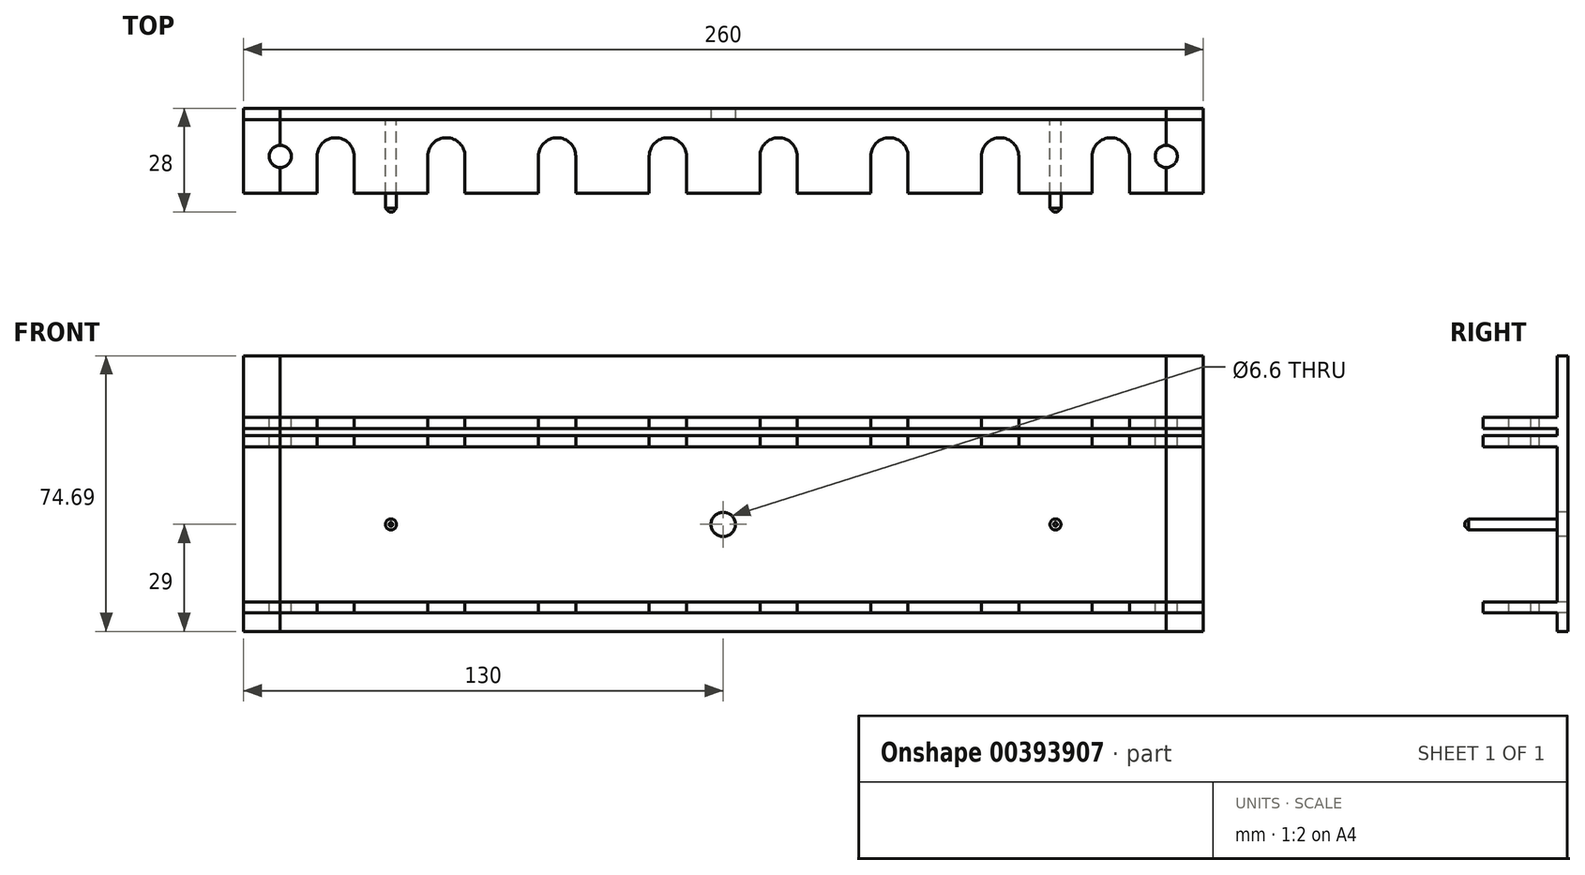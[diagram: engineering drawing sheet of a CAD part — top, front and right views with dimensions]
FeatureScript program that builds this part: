
annotation { "Feature Type Name" : "Feature", "Feature Type Description" : "" }
export const myFeature = defineFeature(function(context is Context, id is Id, definition is map)
    precondition{}
    {
        {
            var Q0;
            Q0=qCreatedBy(makeId("Top.planeOp"),FACE);
            var sketch = newSketch(context, id + "F0", { "sketchPlane" : qUnion([Q0])});
            skLineSegment(sketch, "E0.bottom", {"start": v(15, 10) * mm, "end": v(-15, 10) * mm});
            skLineSegment(sketch, "E0.top", {"start": v(15, -10) * mm, "end": v(-15, -10) * mm});
            skLineSegment(sketch, "E0.left", {"start": v(15, 10) * mm, "end": v(15, -10) * mm});
            skLineSegment(sketch, "E0.right", {"start": v(-15, 10) * mm, "end": v(-15, -10) * mm});
            skPoint(sketch, "E0.middle", {"position": v(0, 0) * mm});
            skSolve(sketch);
        }
        {
            var Q0;
            Q0=makeQuery(id+"F0.imprint","IMPRINT",FACE,{"disambiguationData":[TD([[makeQuery(id+"F0.imprint","IMPRINT",EDGE,{"derivedFrom":sQuery(id+"F0.wireOp",EDGE,"E0.bottom")}),1.0]])]});
            extrude(context, id + "F1", {"entities" : qUnion([Q0]), "oppositeDirection" : true, "depth" : 3 * mm, "offsetDistance" : 25 * mm});
        }
        {
            var Q0;
            Q0=makeQuery(id+"F1.opExtrude","SWEPT_FACE",FACE,{"disambiguationData":[OSD([sQuery(id+"F0.wireOp",EDGE,"E0.bottom")])]});
            var sketch = newSketch(context, id + "F2", { "sketchPlane" : qUnion([Q0])});
            skLineSegment(sketch, "E1.bottom", {"start": v(-15, -53) * mm, "end": v(15, -53) * mm});
            skLineSegment(sketch, "E1.top", {"start": v(-15, 21.69) * mm, "end": v(15, 21.69) * mm});
            skLineSegment(sketch, "E1.left", {"start": v(-15, -53) * mm, "end": v(-15, 21.69) * mm});
            skLineSegment(sketch, "E1.right", {"start": v(15, -53) * mm, "end": v(15, 21.69) * mm});
            skSolve(sketch);
        }
        {
            var Q0;
            {var subQ0=sQuery(id+"F2.wireOp",EDGE,"E1.top");Q0=makeQuery(id+"F2.imprint","IMPRINT",FACE,{"disambiguationData":[TD([[makeQuery(id+"F2.imprint","IMPRINT",EDGE,{"derivedFrom":subQ0}),-1.0]])]});}
            var Q1;
            {var subQ1=sQuery(id+"F0.wireOp",EDGE,"E0.bottom");var subQ2=makeQuery(id+"F1.opExtrude","CAP_EDGE",EDGE,{"disambiguationData":[OSD([subQ1])],"isStart":true});Q1=makeQuery(id+"F2.imprint","IMPRINT",FACE,{"disambiguationData":[TD([[makeQuery(id+"F2.imprint","IMPRINT",EDGE,{"derivedFrom":subQ2}),-1.0]])]});}
            var Q2;
            {var subQ0=sQuery(id+"F2.wireOp",EDGE,"E1.bottom");Q2=makeQuery(id+"F2.imprint","IMPRINT",FACE,{"disambiguationData":[TD([[makeQuery(id+"F2.imprint","IMPRINT",EDGE,{"derivedFrom":subQ0}),1.0]])]});}
            extrude(context, id + "F3", {"entities" : qUnion([Q0, Q1, Q2]), "operationType" : NewBodyOperationType.ADD, "depth" : 3 * mm, "offsetDistance" : 25 * mm});
        }
        {
            var Q0;
            {var subQ1=sQuery(id+"F2.wireOp",EDGE,"E1.left");var subQ3=sQuery(id+"F2.wireOp",EDGE,"E1.top");var subQ4=sQuery(id+"F2.wireOp",EDGE,"E1.right");Q0=makeQuery(id+"F3.boolean.opBoolean","SPLIT",FACE,{"disambiguationData":[TD([makeQuery(id+"F3.opExtrude","SWEPT_FACE",FACE,{"disambiguationData":[OSD([subQ3])]})])],"derivedFrom":makeQuery(id+"F3.opExtrude","CAP_FACE",FACE,{"disambiguationData":[OSD([sQuery(id+"F2.wireOp",EDGE,"E1.bottom"),subQ3,subQ1,subQ4])],"isStart":true})});}
            var sketch = newSketch(context, id + "F4", { "sketchPlane" : qUnion([Q0])});
            skLineSegment(sketch, "E2.bottom", {"start": v(-15, 2) * mm, "end": v(15, 2) * mm});
            skLineSegment(sketch, "E2.top", {"start": v(-15, 5) * mm, "end": v(15, 5) * mm});
            skLineSegment(sketch, "E2.left", {"start": v(-15, 2) * mm, "end": v(-15, 5) * mm});
            skLineSegment(sketch, "E2.right", {"start": v(15, 2) * mm, "end": v(15, 5) * mm});
            skSolve(sketch);
        }
        {
            var Q0;
            Q0=makeQuery(id+"F4.imprint","IMPRINT",FACE,{"disambiguationData":[TD([[makeQuery(id+"F4.imprint","IMPRINT",EDGE,{"derivedFrom":sQuery(id+"F4.wireOp",EDGE,"E2.bottom")}),1.0]])]});
            extrude(context, id + "F5", {"entities" : qUnion([Q0]), "operationType" : NewBodyOperationType.ADD, "depth" : 20 * mm, "offsetDistance" : 25 * mm});
        }
        {
            var Q0;
            Q0=makeQuery(id+"F1.opExtrude","SWEPT_BODY",BODY,{"disambiguationData":[OSD([sQuery(id+"F0.wireOp",EDGE,"E0.bottom"),sQuery(id+"F0.wireOp",EDGE,"E0.top"),sQuery(id+"F0.wireOp",EDGE,"E0.left"),sQuery(id+"F0.wireOp",EDGE,"E0.right")])]});
            var Q1;
            Q1=makeQuery(id+"F5.boolean.opBoolean","MERGE",FACE,{"derivedFrom":[makeQuery(id+"F3.boolean.opBoolean","MERGE",FACE,{"derivedFrom":[makeQuery(id+"F1.opExtrude","SWEPT_FACE",FACE,{"disambiguationData":[OSD([sQuery(id+"F0.wireOp",EDGE,"E0.left")])]}),makeQuery(id+"F3.opExtrude","SWEPT_FACE",FACE,{"disambiguationData":[OSD([sQuery(id+"F2.wireOp",EDGE,"E1.left")])]})]}),makeQuery(id+"F5.opExtrude","SWEPT_FACE",FACE,{"disambiguationData":[OSD([sQuery(id+"F4.wireOp",EDGE,"E2.right")])]})]});
            mirror(context, id + "F6", {"operationType" : NewBodyOperationType.ADD, "entities" : qUnion([Q0]), "mirrorPlane" : qUnion([Q1])});
        }
        {
            var Q0;
            Q0=makeQuery(id+"F1.opExtrude","SWEPT_BODY",BODY,{"disambiguationData":[OSD([sQuery(id+"F0.wireOp",EDGE,"E0.bottom"),sQuery(id+"F0.wireOp",EDGE,"E0.top"),sQuery(id+"F0.wireOp",EDGE,"E0.left"),sQuery(id+"F0.wireOp",EDGE,"E0.right")])]});
            var Q1;
            Q1=makeQuery(id+"F6.opPattern","COPY",FACE,{"derivedFrom":makeQuery(id+"F5.boolean.opBoolean","MERGE",FACE,{"derivedFrom":[makeQuery(id+"F3.boolean.opBoolean","MERGE",FACE,{"derivedFrom":[makeQuery(id+"F1.opExtrude","SWEPT_FACE",FACE,{"disambiguationData":[OSD([sQuery(id+"F0.wireOp",EDGE,"E0.right")])]}),makeQuery(id+"F3.opExtrude","SWEPT_FACE",FACE,{"disambiguationData":[OSD([sQuery(id+"F2.wireOp",EDGE,"E1.right")])]})]}),makeQuery(id+"F5.opExtrude","SWEPT_FACE",FACE,{"disambiguationData":[OSD([sQuery(id+"F4.wireOp",EDGE,"E2.left")])]})]}),"instanceName":"1"});
            mirror(context, id + "F7", {"operationType" : NewBodyOperationType.ADD, "entities" : qUnion([Q0]), "mirrorPlane" : qUnion([Q1])});
        }
        {
            var Q0;
            Q0=makeQuery(id+"F1.opExtrude","SWEPT_BODY",BODY,{"disambiguationData":[OSD([sQuery(id+"F0.wireOp",EDGE,"E0.bottom"),sQuery(id+"F0.wireOp",EDGE,"E0.top"),sQuery(id+"F0.wireOp",EDGE,"E0.left"),sQuery(id+"F0.wireOp",EDGE,"E0.right")])]});
            var Q1;
            Q1=makeQuery(id+"F7.opPattern","COPY",FACE,{"derivedFrom":makeQuery(id+"F5.boolean.opBoolean","MERGE",FACE,{"derivedFrom":[makeQuery(id+"F3.boolean.opBoolean","MERGE",FACE,{"derivedFrom":[makeQuery(id+"F1.opExtrude","SWEPT_FACE",FACE,{"disambiguationData":[OSD([sQuery(id+"F0.wireOp",EDGE,"E0.right")])]}),makeQuery(id+"F3.opExtrude","SWEPT_FACE",FACE,{"disambiguationData":[OSD([sQuery(id+"F2.wireOp",EDGE,"E1.right")])]})]}),makeQuery(id+"F5.opExtrude","SWEPT_FACE",FACE,{"disambiguationData":[OSD([sQuery(id+"F4.wireOp",EDGE,"E2.left")])]})]}),"instanceName":"1"});
            mirror(context, id + "F8", {"operationType" : NewBodyOperationType.ADD, "entities" : qUnion([Q0]), "mirrorPlane" : qUnion([Q1])});
        }
        {
            var Q0;
            {var subQ0=makeQuery(id+"F1.opExtrude","CAP_FACE",FACE,{"disambiguationData":[OSD([sQuery(id+"F0.wireOp",EDGE,"E0.bottom"),sQuery(id+"F0.wireOp",EDGE,"E0.top"),sQuery(id+"F0.wireOp",EDGE,"E0.left"),sQuery(id+"F0.wireOp",EDGE,"E0.right")])],"isStart":false});var subQ1=makeQuery(id+"F6.boolean.opBoolean","MERGE",FACE,{"derivedFrom":[subQ0,makeQuery(id+"F6.opPattern","COPY",FACE,{"derivedFrom":subQ0,"instanceName":"1"})]});var subQ2=makeQuery(id+"F7.boolean.opBoolean","MERGE",FACE,{"derivedFrom":[subQ1,makeQuery(id+"F7.opPattern","COPY",FACE,{"derivedFrom":subQ1,"instanceName":"1"})]});Q0=makeQuery(id+"F8.boolean.opBoolean","MERGE",FACE,{"derivedFrom":[subQ2,makeQuery(id+"F8.opPattern","COPY",FACE,{"derivedFrom":subQ2,"instanceName":"1"})]});}
            cPlane(context, id + "F9", {"entities" : qUnion([Q0]), "cplaneType" : CPlaneType.OFFSET, "offset" : 45 * mm, "width" : 150 * mm, "height" : 150 * mm});
        }
        {
            var Q0;
            Q0=qCreatedBy(id+"F9.planeOp",FACE);
            var sketch = newSketch(context, id + "F10", { "sketchPlane" : qUnion([Q0])});
            skLineSegment(sketch, "E3.bottom", {"start": v(-15, -13) * mm, "end": v(225, -13) * mm});
            skLineSegment(sketch, "E3.top", {"start": v(-15, 10) * mm, "end": v(225, 10) * mm});
            skLineSegment(sketch, "E3.left", {"start": v(-15, -13) * mm, "end": v(-15, 10) * mm});
            skLineSegment(sketch, "E3.right", {"start": v(225, -13) * mm, "end": v(225, 10) * mm});
            skSolve(sketch);
        }
        {
            var Q0;
            {var subQ0=sQuery(id+"F10.wireOp",EDGE,"E3.top");Q0=makeQuery(id+"F10.imprint","IMPRINT",FACE,{"disambiguationData":[TD([[makeQuery(id+"F10.imprint","IMPRINT",EDGE,{"derivedFrom":subQ0}),-1.0]])]});}
            extrude(context, id + "F11", {"entities" : qUnion([Q0]), "oppositeDirection" : true, "depth" : 3 * mm, "offsetDistance" : 25 * mm});
        }
        {
            var Q0;
            Q0=makeQuery(id+"F11.opExtrude","CAP_FACE",FACE,{"disambiguationData":[OSD([sQuery(id+"F10.wireOp",EDGE,"E3.bottom"),sQuery(id+"F10.wireOp",EDGE,"E3.top"),sQuery(id+"F10.wireOp",EDGE,"E3.left"),sQuery(id+"F10.wireOp",EDGE,"E3.right")])],"isStart":true});
            var sketch = newSketch(context, id + "F12", { "sketchPlane" : qUnion([Q0])});
            skArc(sketch, "E4", {"start": v(-5.05, 0) * mm, "mid": v(0, -5.05) * mm, "end": v(5.05, 0) * mm});
            skLineSegment(sketch, "E5.bottom", {"start": v(-5.05, 0) * mm, "end": v(5.05, 0) * mm});
            skLineSegment(sketch, "E5.top", {"start": v(-5.05, 10) * mm, "end": v(5.05, 10) * mm});
            skLineSegment(sketch, "E5.left", {"start": v(-5.05, 0) * mm, "end": v(-5.05, 10) * mm});
            skLineSegment(sketch, "E5.right", {"start": v(5.05, 0) * mm, "end": v(5.05, 10) * mm});
            skLineSegment(sketch, "E6", {"start": v(15, 10) * mm, "end": v(15, -13) * mm, "construction": true});
            skLineSegment(sketch, "E7.1.0.0", {"start": v(35.05, 0) * mm, "end": v(35.05, 10) * mm});
            skArc(sketch, "E7.1.0.1", {"start": v(24.95, 0) * mm, "mid": v(30, -5.05) * mm, "end": v(35.05, 0) * mm});
            skLineSegment(sketch, "E7.1.0.2", {"start": v(24.95, 0) * mm, "end": v(24.95, 10) * mm});
            skLineSegment(sketch, "E7.2.0.0", {"start": v(65.05, 0) * mm, "end": v(65.05, 10) * mm});
            skArc(sketch, "E7.2.0.1", {"start": v(54.95, 0) * mm, "mid": v(60, -5.05) * mm, "end": v(65.05, 0) * mm});
            skLineSegment(sketch, "E7.2.0.2", {"start": v(54.95, 0) * mm, "end": v(54.95, 10) * mm});
            skLineSegment(sketch, "E7.3.0.0", {"start": v(95.05, 0) * mm, "end": v(95.05, 10) * mm});
            skArc(sketch, "E7.3.0.1", {"start": v(84.95, 0) * mm, "mid": v(90, -5.05) * mm, "end": v(95.05, 0) * mm});
            skLineSegment(sketch, "E7.3.0.2", {"start": v(84.95, 0) * mm, "end": v(84.95, 10) * mm});
            skLineSegment(sketch, "E7.4.0.0", {"start": v(125.05, 0) * mm, "end": v(125.05, 10) * mm});
            skArc(sketch, "E7.4.0.1", {"start": v(114.95, 0) * mm, "mid": v(120, -5.05) * mm, "end": v(125.05, 0) * mm});
            skLineSegment(sketch, "E7.4.0.2", {"start": v(114.95, 0) * mm, "end": v(114.95, 10) * mm});
            skLineSegment(sketch, "E7.5.0.0", {"start": v(155.05, 0) * mm, "end": v(155.05, 10) * mm});
            skArc(sketch, "E7.5.0.1", {"start": v(144.95, 0) * mm, "mid": v(150, -5.05) * mm, "end": v(155.05, 0) * mm});
            skLineSegment(sketch, "E7.5.0.2", {"start": v(144.95, 0) * mm, "end": v(144.95, 10) * mm});
            skLineSegment(sketch, "E7.6.0.0", {"start": v(185.05, 0) * mm, "end": v(185.05, 10) * mm});
            skArc(sketch, "E7.6.0.1", {"start": v(174.95, 0) * mm, "mid": v(180, -5.05) * mm, "end": v(185.05, 0) * mm});
            skLineSegment(sketch, "E7.6.0.2", {"start": v(174.95, 0) * mm, "end": v(174.95, 10) * mm});
            skLineSegment(sketch, "E7.7.0.0", {"start": v(215.05, 0) * mm, "end": v(215.05, 10) * mm});
            skArc(sketch, "E7.7.0.1", {"start": v(204.95, 0) * mm, "mid": v(210, -5.05) * mm, "end": v(215.05, 0) * mm});
            skLineSegment(sketch, "E7.7.0.2", {"start": v(204.95, 0) * mm, "end": v(204.95, 10) * mm});
            skLineSegment(sketch, "E7.direction1", {"start": v(-5.05, 0) * mm, "end": v(24.95, 0) * mm, "construction": true});
            skSolve(sketch);
        }
        {
            var Q0;
            Q0=makeQuery(id+"F12.imprint","IMPRINT",FACE,{"disambiguationData":[TD([[makeQuery(id+"F12.imprint","IMPRINT",EDGE,{"derivedFrom":sQuery(id+"F12.wireOp",EDGE,"E5.bottom")}),1.0]])]});
            var Q1;
            Q1=makeQuery(id+"F12.imprint","IMPRINT",FACE,{"disambiguationData":[TD([[makeQuery(id+"F12.imprint","IMPRINT",EDGE,{"derivedFrom":sQuery(id+"F12.wireOp",EDGE,"E4")}),1.0]])]});
            var Q2;
            {var subQ0=sQuery(id+"F12.wireOp",EDGE,"E7.1.0.0");Q2=makeQuery(id+"F12.imprint","IMPRINT",FACE,{"disambiguationData":[TD([[makeQuery(id+"F12.imprint","IMPRINT",EDGE,{"derivedFrom":subQ0}),1.0]])]});}
            var Q3;
            {var subQ0=sQuery(id+"F12.wireOp",EDGE,"E7.2.0.0");Q3=makeQuery(id+"F12.imprint","IMPRINT",FACE,{"disambiguationData":[TD([[makeQuery(id+"F12.imprint","IMPRINT",EDGE,{"derivedFrom":subQ0}),1.0]])]});}
            var Q4;
            {var subQ0=sQuery(id+"F12.wireOp",EDGE,"E7.3.0.0");Q4=makeQuery(id+"F12.imprint","IMPRINT",FACE,{"disambiguationData":[TD([[makeQuery(id+"F12.imprint","IMPRINT",EDGE,{"derivedFrom":subQ0}),1.0]])]});}
            var Q5;
            {var subQ0=sQuery(id+"F12.wireOp",EDGE,"E7.4.0.0");Q5=makeQuery(id+"F12.imprint","IMPRINT",FACE,{"disambiguationData":[TD([[makeQuery(id+"F12.imprint","IMPRINT",EDGE,{"derivedFrom":subQ0}),1.0]])]});}
            var Q6;
            {var subQ0=sQuery(id+"F12.wireOp",EDGE,"E7.5.0.0");Q6=makeQuery(id+"F12.imprint","IMPRINT",FACE,{"disambiguationData":[TD([[makeQuery(id+"F12.imprint","IMPRINT",EDGE,{"derivedFrom":subQ0}),1.0]])]});}
            var Q7;
            {var subQ0=sQuery(id+"F12.wireOp",EDGE,"E7.6.0.0");Q7=makeQuery(id+"F12.imprint","IMPRINT",FACE,{"disambiguationData":[TD([[makeQuery(id+"F12.imprint","IMPRINT",EDGE,{"derivedFrom":subQ0}),1.0]])]});}
            var Q8;
            {var subQ0=sQuery(id+"F12.wireOp",EDGE,"E7.7.0.0");Q8=makeQuery(id+"F12.imprint","IMPRINT",FACE,{"disambiguationData":[TD([[makeQuery(id+"F12.imprint","IMPRINT",EDGE,{"derivedFrom":subQ0}),1.0]])]});}
            var Q9;
            {var subQ0=makeQuery(id+"F5.opExtrude","SWEPT_FACE",FACE,{"disambiguationData":[OSD([sQuery(id+"F4.wireOp",EDGE,"E2.top")])]});var subQ1=makeQuery(id+"F6.boolean.opBoolean","MERGE",FACE,{"derivedFrom":[subQ0,makeQuery(id+"F6.opPattern","COPY",FACE,{"derivedFrom":subQ0,"instanceName":"1"})]});var subQ2=makeQuery(id+"F7.boolean.opBoolean","MERGE",FACE,{"derivedFrom":[subQ1,makeQuery(id+"F7.opPattern","COPY",FACE,{"derivedFrom":subQ1,"instanceName":"1"})]});Q9=makeQuery(id+"F8.boolean.opBoolean","MERGE",FACE,{"derivedFrom":[subQ2,makeQuery(id+"F8.opPattern","COPY",FACE,{"derivedFrom":subQ2,"instanceName":"1"})]});}
            extrude(context, id + "F13", {"entities" : qUnion([Q0, Q1, Q2, Q3, Q4, Q5, Q6, Q7, Q8]), "operationType" : NewBodyOperationType.REMOVE, "oppositeDirection" : true, "depth" : 72 * mm, "endBoundEntityFace" : qUnion([Q9]), "offsetDistance" : 25 * mm});
        }
        {
            var Q0;
            {var subQ0=sQuery(id+"F2.wireOp",EDGE,"E1.bottom");var subQ2=sQuery(id+"F2.wireOp",EDGE,"E1.left");var subQ4=sQuery(id+"F2.wireOp",EDGE,"E1.right");var subQ5=makeQuery(id+"F3.boolean.opBoolean","SPLIT",FACE,{"disambiguationData":[TD([makeQuery(id+"F3.opExtrude","SWEPT_FACE",FACE,{"disambiguationData":[OSD([subQ0])]})])],"derivedFrom":makeQuery(id+"F3.opExtrude","CAP_FACE",FACE,{"disambiguationData":[OSD([subQ0,sQuery(id+"F2.wireOp",EDGE,"E1.top"),subQ2,subQ4])],"isStart":true})});var subQ6=makeQuery(id+"F6.boolean.opBoolean","MERGE",FACE,{"derivedFrom":[subQ5,makeQuery(id+"F6.opPattern","COPY",FACE,{"derivedFrom":subQ5,"instanceName":"1"})]});var subQ7=makeQuery(id+"F7.boolean.opBoolean","MERGE",FACE,{"derivedFrom":[subQ6,makeQuery(id+"F7.opPattern","COPY",FACE,{"derivedFrom":subQ6,"instanceName":"1"})]});Q0=makeQuery(id+"F8.boolean.opBoolean","MERGE",FACE,{"derivedFrom":[subQ7,makeQuery(id+"F8.opPattern","COPY",FACE,{"derivedFrom":subQ7,"instanceName":"1"})]});}
            var sketch = newSketch(context, id + "F14", { "sketchPlane" : qUnion([Q0])});
            skCircle(sketch, "E8", {"center": v(105, -24) * mm, "radius": 3.25 * mm});
            skPoint(sketch, "E8.centerSnap0", {"position": v(105, -3) * mm});
            skSolve(sketch);
        }
        {
            var Q0;
            Q0=sQuery(id+"F14.wireOp",VERTEX,"E8.center");
            var Q1;
            Q1=makeQuery(id+"F1.opExtrude","SWEPT_BODY",BODY,{"disambiguationData":[OSD([sQuery(id+"F0.wireOp",EDGE,"E0.bottom"),sQuery(id+"F0.wireOp",EDGE,"E0.top"),sQuery(id+"F0.wireOp",EDGE,"E0.left"),sQuery(id+"F0.wireOp",EDGE,"E0.right")])]});
            hole(context, id + "F15", {"style" : HoleStyle.SIMPLE, "endStyle" : HoleEndStyle.BLIND, "standardTappedOrClearance" : lookupTablePath({ "standard" : "ISO", "fit" : "Normal", "size" : "M6", "type" : "Clearance" }), "standardBlindInLast" : lookupTablePath({ "fit" : "Standard", "standard" : "ISO", "size" : "M6", "type" : "Clearance" }), "holeDiameter" : 6.6 * mm, "majorDiameter" : 5 * mm, "holeDepth" : 21.5 * mm, "tappedDepth" : 12 * mm, "tapClearance" : 3, "locations" : qUnion([Q0]), "scope" : qUnion([Q1])});
        }
        {
            var Q0;
            {var subQ0=sQuery(id+"F2.wireOp",EDGE,"E1.bottom");var subQ2=sQuery(id+"F2.wireOp",EDGE,"E1.left");var subQ4=sQuery(id+"F2.wireOp",EDGE,"E1.right");var subQ5=makeQuery(id+"F3.boolean.opBoolean","SPLIT",FACE,{"disambiguationData":[TD([makeQuery(id+"F3.opExtrude","SWEPT_FACE",FACE,{"disambiguationData":[OSD([subQ0])]})])],"derivedFrom":makeQuery(id+"F3.opExtrude","CAP_FACE",FACE,{"disambiguationData":[OSD([subQ0,sQuery(id+"F2.wireOp",EDGE,"E1.top"),subQ2,subQ4])],"isStart":true})});var subQ6=makeQuery(id+"F6.boolean.opBoolean","MERGE",FACE,{"derivedFrom":[subQ5,makeQuery(id+"F6.opPattern","COPY",FACE,{"derivedFrom":subQ5,"instanceName":"1"})]});var subQ7=makeQuery(id+"F7.boolean.opBoolean","MERGE",FACE,{"derivedFrom":[subQ6,makeQuery(id+"F7.opPattern","COPY",FACE,{"derivedFrom":subQ6,"instanceName":"1"})]});Q0=makeQuery(id+"F8.boolean.opBoolean","MERGE",FACE,{"derivedFrom":[subQ7,makeQuery(id+"F8.opPattern","COPY",FACE,{"derivedFrom":subQ7,"instanceName":"1"})]});}
            var sketch = newSketch(context, id + "F16", { "sketchPlane" : qUnion([Q0])});
            skCircle(sketch, "E9", {"center": v(195, -24) * mm, "radius": 1.5 * mm});
            skCircle(sketch, "E10", {"center": v(15, -24) * mm, "radius": 1.5 * mm});
            skSolve(sketch);
        }
        {
            var Q0;
            Q0=makeQuery(id+"F16.imprint","IMPRINT",FACE,{"disambiguationData":[TD([[makeQuery(id+"F16.imprint","IMPRINT",EDGE,{"derivedFrom":sQuery(id+"F16.wireOp",EDGE,"E10")}),1.0]])]});
            var Q1;
            Q1=makeQuery(id+"F16.imprint","IMPRINT",FACE,{"disambiguationData":[TD([[makeQuery(id+"F16.imprint","IMPRINT",EDGE,{"derivedFrom":sQuery(id+"F16.wireOp",EDGE,"E9")}),1.0]])]});
            extrude(context, id + "F17", {"entities" : qUnion([Q0, Q1]), "operationType" : NewBodyOperationType.ADD, "depth" : 25 * mm, "offsetDistance" : 25 * mm});
        }
        {
            var Q0;
            Q0=makeQuery(id+"F17.opExtrude","CAP_EDGE",EDGE,{"disambiguationData":[OSD([sQuery(id+"F16.wireOp",EDGE,"E10")])],"isStart":false});
            var Q1;
            Q1=makeQuery(id+"F17.opExtrude","CAP_EDGE",EDGE,{"disambiguationData":[OSD([sQuery(id+"F16.wireOp",EDGE,"E9")])],"isStart":false});
            chamfer(context, id + "F18", {"entities" : qUnion([Q0, Q1]), "width" : 1 * mm, "tangentPropagation" : true});
        }
        {
            var Q0;
            Q0=makeQuery(id+"F8.opPattern","COPY",FACE,{"derivedFrom":makeQuery(id+"F5.boolean.opBoolean","MERGE",FACE,{"derivedFrom":[makeQuery(id+"F3.boolean.opBoolean","MERGE",FACE,{"derivedFrom":[makeQuery(id+"F1.opExtrude","SWEPT_FACE",FACE,{"disambiguationData":[OSD([sQuery(id+"F0.wireOp",EDGE,"E0.right")])]}),makeQuery(id+"F3.opExtrude","SWEPT_FACE",FACE,{"disambiguationData":[OSD([sQuery(id+"F2.wireOp",EDGE,"E1.right")])]})]}),makeQuery(id+"F5.opExtrude","SWEPT_FACE",FACE,{"disambiguationData":[OSD([sQuery(id+"F4.wireOp",EDGE,"E2.left")])]})]}),"instanceName":"1"});
            var sketch = newSketch(context, id + "F19", { "sketchPlane" : qUnion([Q0])});
            skLineSegment(sketch, "E11", {"start": v(10, 21.69) * mm, "end": v(13, 21.69) * mm});
            skLineSegment(sketch, "E12", {"start": v(13, 21.69) * mm, "end": v(13, -53) * mm});
            skLineSegment(sketch, "E13", {"start": v(13, -53) * mm, "end": v(10, -53) * mm});
            skLineSegment(sketch, "E14", {"start": v(10, -53) * mm, "end": v(10, -48) * mm});
            skLineSegment(sketch, "E15", {"start": v(10, -48) * mm, "end": v(-10, -48) * mm});
            skLineSegment(sketch, "E16", {"start": v(-10, -48) * mm, "end": v(-10, -45) * mm});
            skLineSegment(sketch, "E17", {"start": v(-10, -45) * mm, "end": v(10, -45) * mm});
            skLineSegment(sketch, "E18", {"start": v(10, -45) * mm, "end": v(10, -3) * mm});
            skLineSegment(sketch, "E19", {"start": v(10, -3) * mm, "end": v(-10, -3) * mm});
            skLineSegment(sketch, "E20", {"start": v(-10, -3) * mm, "end": v(-10, 0) * mm});
            skLineSegment(sketch, "E21", {"start": v(-10, 0) * mm, "end": v(10, 0) * mm});
            skLineSegment(sketch, "E22", {"start": v(10, 0) * mm, "end": v(10, 2) * mm});
            skLineSegment(sketch, "E23", {"start": v(10, 2) * mm, "end": v(-10, 2) * mm});
            skLineSegment(sketch, "E24", {"start": v(-10, 2) * mm, "end": v(-10, 5) * mm});
            skLineSegment(sketch, "E25", {"start": v(-10, 5) * mm, "end": v(10, 5) * mm});
            skLineSegment(sketch, "E26", {"start": v(10, 5) * mm, "end": v(10, 21.69) * mm});
            skSolve(sketch);
        }
        {
            var Q0;
            Q0=makeQuery(id+"F19.imprint","IMPRINT",FACE,{"disambiguationData":[TD([[makeQuery(id+"F19.imprint","IMPRINT",EDGE,{"derivedFrom":sQuery(id+"F19.wireOp",EDGE,"E11")}),1.0]])]});
            var Q1;
            {var subQ0=sQuery(id+"F19.wireOp",EDGE,"E15");Q1=makeQuery(id+"F19.imprint","IMPRINT",FACE,{"disambiguationData":[TD([[makeQuery(id+"F19.imprint","IMPRINT",EDGE,{"derivedFrom":subQ0}),-1.0]])]});}
            extrude(context, id + "F20", {"entities" : qUnion([Q0, Q1]), "depth" : 10 * mm, "offsetDistance" : 25 * mm});
        }
        {
            var Q0;
            Q0=makeQuery(id+"F5.boolean.opBoolean","MERGE",FACE,{"derivedFrom":[makeQuery(id+"F3.boolean.opBoolean","MERGE",FACE,{"derivedFrom":[makeQuery(id+"F1.opExtrude","SWEPT_FACE",FACE,{"disambiguationData":[OSD([sQuery(id+"F0.wireOp",EDGE,"E0.right")])]}),makeQuery(id+"F3.opExtrude","SWEPT_FACE",FACE,{"disambiguationData":[OSD([sQuery(id+"F2.wireOp",EDGE,"E1.right")])]})]}),makeQuery(id+"F5.opExtrude","SWEPT_FACE",FACE,{"disambiguationData":[OSD([sQuery(id+"F4.wireOp",EDGE,"E2.left")])]})]});
            var sketch = newSketch(context, id + "F21", { "sketchPlane" : qUnion([Q0])});
            skLineSegment(sketch, "E27", {"start": v(-10, 21.69) * mm, "end": v(-13, 21.69) * mm});
            skLineSegment(sketch, "E28", {"start": v(-13, 21.69) * mm, "end": v(-13, -53) * mm});
            skLineSegment(sketch, "E29", {"start": v(-13, -53) * mm, "end": v(-10, -53) * mm});
            skLineSegment(sketch, "E30", {"start": v(-10, -53) * mm, "end": v(-10, -48) * mm});
            skLineSegment(sketch, "E31", {"start": v(-10, -48) * mm, "end": v(10, -48) * mm});
            skLineSegment(sketch, "E32", {"start": v(10, -48) * mm, "end": v(10, -45) * mm});
            skLineSegment(sketch, "E33", {"start": v(10, -45) * mm, "end": v(-10, -45) * mm});
            skLineSegment(sketch, "E34", {"start": v(-10, -45) * mm, "end": v(-10, -3) * mm});
            skLineSegment(sketch, "E35", {"start": v(-10, -3) * mm, "end": v(10, -3) * mm});
            skLineSegment(sketch, "E36", {"start": v(10, -3) * mm, "end": v(10, 0) * mm});
            skLineSegment(sketch, "E37", {"start": v(10, 0) * mm, "end": v(-10, 0) * mm});
            skLineSegment(sketch, "E38", {"start": v(-10, 0) * mm, "end": v(-10, 2) * mm});
            skLineSegment(sketch, "E39", {"start": v(-10, 2) * mm, "end": v(10, 2) * mm});
            skLineSegment(sketch, "E40", {"start": v(10, 2) * mm, "end": v(10, 5) * mm});
            skLineSegment(sketch, "E41", {"start": v(10, 5) * mm, "end": v(-10, 5) * mm});
            skLineSegment(sketch, "E42", {"start": v(-10, 5) * mm, "end": v(-10, 21.69) * mm});
            skSolve(sketch);
        }
        {
            var Q0;
            Q0=makeQuery(id+"F21.imprint","IMPRINT",FACE,{"disambiguationData":[TD([[makeQuery(id+"F21.imprint","IMPRINT",EDGE,{"derivedFrom":sQuery(id+"F21.wireOp",EDGE,"E27")}),-1.0]])]});
            var Q1;
            {var subQ0=sQuery(id+"F21.wireOp",EDGE,"E31");Q1=makeQuery(id+"F21.imprint","IMPRINT",FACE,{"disambiguationData":[TD([[makeQuery(id+"F21.imprint","IMPRINT",EDGE,{"derivedFrom":subQ0}),1.0]])]});}
            extrude(context, id + "F22", {"entities" : qUnion([Q0, Q1]), "depth" : 10 * mm, "offsetDistance" : 25 * mm});
        }
        {
            var Q0;
            {var subQ0=makeQuery(id+"F5.opExtrude","SWEPT_FACE",FACE,{"disambiguationData":[OSD([sQuery(id+"F4.wireOp",EDGE,"E2.top")])]});var subQ1=makeQuery(id+"F6.boolean.opBoolean","MERGE",FACE,{"derivedFrom":[subQ0,makeQuery(id+"F6.opPattern","COPY",FACE,{"derivedFrom":subQ0,"instanceName":"1"})]});var subQ2=makeQuery(id+"F7.boolean.opBoolean","MERGE",FACE,{"derivedFrom":[subQ1,makeQuery(id+"F7.opPattern","COPY",FACE,{"derivedFrom":subQ1,"instanceName":"1"})]});Q0=makeQuery(id+"F8.boolean.opBoolean","MERGE",FACE,{"derivedFrom":[subQ2,makeQuery(id+"F8.opPattern","COPY",FACE,{"derivedFrom":subQ2,"instanceName":"1"})]});}
            var sketch = newSketch(context, id + "F23", { "sketchPlane" : qUnion([Q0])});
            skCircle(sketch, "E43", {"center": v(-15, 0) * mm, "radius": 3 * mm});
            skCircle(sketch, "E44", {"center": v(225, 0) * mm, "radius": 3 * mm});
            skSolve(sketch);
        }
        {
            var Q0;
            {var subQ0=sQuery(id+"F23.wireOp",EDGE,"E43");var subQ1=makeQuery(id+"F5.opExtrude","SWEPT_EDGE",EDGE,{"disambiguationData":[OSD([sQuery(id+"F2.wireOp",EDGE,"E1.right"),sQuery(id+"F4.wireOp",EDGE,"E2.top"),sQuery(id+"F4.wireOp",EDGE,"E2.left")])]});var subQ2=makeQuery(id+"F23.imprint","INTERSECT",VERTEX,{"disambiguationData":[OD(0.0)],"derivedFrom":[subQ1,subQ0]});Q0=makeQuery(id+"F23.imprint","IMPRINT",FACE,{"disambiguationData":[TD([[makeQuery(id+"F23.imprint","IMPRINT",EDGE,{"disambiguationData":[TD([[subQ2,1.0]])],"derivedFrom":subQ0}),1.0]])]});}
            var Q1;
            {var subQ0=sQuery(id+"F23.wireOp",EDGE,"E43");var subQ1=makeQuery(id+"F5.opExtrude","SWEPT_EDGE",EDGE,{"disambiguationData":[OSD([sQuery(id+"F2.wireOp",EDGE,"E1.right"),sQuery(id+"F4.wireOp",EDGE,"E2.top"),sQuery(id+"F4.wireOp",EDGE,"E2.left")])]});var subQ2=makeQuery(id+"F23.imprint","INTERSECT",VERTEX,{"disambiguationData":[OD(0.0)],"derivedFrom":[subQ1,subQ0]});Q1=makeQuery(id+"F23.imprint","IMPRINT",FACE,{"disambiguationData":[TD([[makeQuery(id+"F23.imprint","IMPRINT",EDGE,{"disambiguationData":[TD([[subQ2,-1.0]])],"derivedFrom":subQ0}),1.0]])]});}
            var Q2;
            {var subQ0=sQuery(id+"F23.wireOp",EDGE,"E44");var subQ1=makeQuery(id+"F8.opPattern","COPY",EDGE,{"derivedFrom":makeQuery(id+"F5.opExtrude","SWEPT_EDGE",EDGE,{"disambiguationData":[OSD([sQuery(id+"F2.wireOp",EDGE,"E1.right"),sQuery(id+"F4.wireOp",EDGE,"E2.top"),sQuery(id+"F4.wireOp",EDGE,"E2.left")])]}),"instanceName":"1"});var subQ2=makeQuery(id+"F23.imprint","INTERSECT",VERTEX,{"disambiguationData":[OD(0.0)],"derivedFrom":[subQ1,subQ0]});Q2=makeQuery(id+"F23.imprint","IMPRINT",FACE,{"disambiguationData":[TD([[makeQuery(id+"F23.imprint","IMPRINT",EDGE,{"disambiguationData":[TD([[subQ2,-1.0]])],"derivedFrom":subQ0}),1.0]])]});}
            var Q3;
            {var subQ0=sQuery(id+"F23.wireOp",EDGE,"E44");var subQ1=makeQuery(id+"F8.opPattern","COPY",EDGE,{"derivedFrom":makeQuery(id+"F5.opExtrude","SWEPT_EDGE",EDGE,{"disambiguationData":[OSD([sQuery(id+"F2.wireOp",EDGE,"E1.right"),sQuery(id+"F4.wireOp",EDGE,"E2.top"),sQuery(id+"F4.wireOp",EDGE,"E2.left")])]}),"instanceName":"1"});var subQ2=makeQuery(id+"F23.imprint","INTERSECT",VERTEX,{"disambiguationData":[OD(0.0)],"derivedFrom":[subQ1,subQ0]});Q3=makeQuery(id+"F23.imprint","IMPRINT",FACE,{"disambiguationData":[TD([[makeQuery(id+"F23.imprint","IMPRINT",EDGE,{"disambiguationData":[TD([[subQ2,1.0]])],"derivedFrom":subQ0}),1.0]])]});}
            extrude(context, id + "F24", {"entities" : qUnion([Q0, Q1, Q2, Q3]), "operationType" : NewBodyOperationType.REMOVE, "oppositeDirection" : true, "depth" : 60 * mm, "offsetDistance" : 25 * mm});
        }
    });
